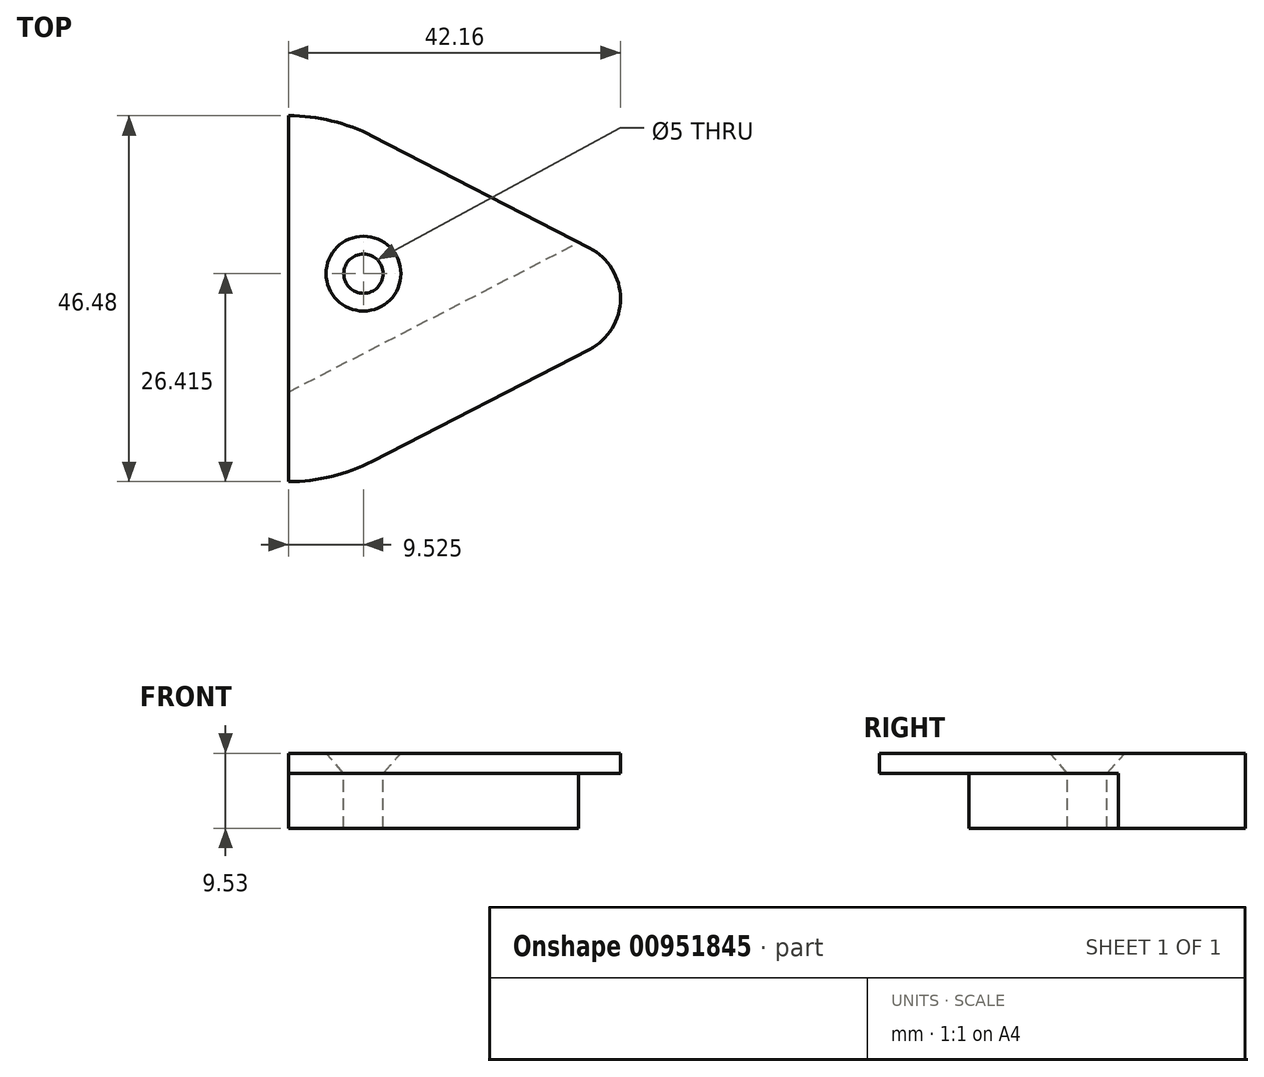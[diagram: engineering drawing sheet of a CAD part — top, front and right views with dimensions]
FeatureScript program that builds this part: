
annotation { "Feature Type Name" : "Feature", "Feature Type Description" : "" }
export const myFeature = defineFeature(function(context is Context, id is Id, definition is map)
    precondition{}
    {
        {
            var Q0;
            Q0=qCreatedBy(makeId("Top.planeOp"),FACE);
            var sketch = newSketch(context, id + "F0", { "sketchPlane" : qUnion([Q0])});
            skArc(sketch, "E0", {"start": v(0, -23.62) * mm, "mid": v(5.57, -22.96) * mm, "end": v(10.82, -21) * mm, "construction": true});
            skArc(sketch, "E1", {"start": v(38.42, -6.77) * mm, "mid": v(42.55, 0) * mm, "end": v(38.42, 6.77) * mm, "construction": true});
            skLineSegment(sketch, "E2", {"start": v(10.82, 21) * mm, "end": v(38.42, 6.77) * mm, "construction": true});
            skLineSegment(sketch, "E3", {"start": v(10.82, -21) * mm, "end": v(38.42, -6.77) * mm, "construction": true});
            skLineSegment(sketch, "E4", {"start": v(0, 23.24) * mm, "end": v(0, -23.24) * mm});
            skArc(sketch, "E5.trimOffspring", {"start": v(10.82, 21) * mm, "mid": v(5.57, 22.96) * mm, "end": v(0, 23.62) * mm, "construction": true});
            skArc(sketch, "E6.0", {"start": v(10.65, 20.66) * mm, "mid": v(5.48, 22.59) * mm, "end": v(0, 23.24) * mm});
            skArc(sketch, "E6.1", {"start": v(0, -23.24) * mm, "mid": v(5.48, -22.59) * mm, "end": v(10.65, -20.66) * mm});
            skLineSegment(sketch, "E6.2", {"start": v(10.65, -20.66) * mm, "end": v(38.24, -6.43) * mm});
            skArc(sketch, "E6.3", {"start": v(38.24, -6.43) * mm, "mid": v(42.16, 0) * mm, "end": v(38.24, 6.43) * mm});
            skLineSegment(sketch, "E6.4", {"start": v(10.65, 20.66) * mm, "end": v(38.24, 6.43) * mm});
            skSolve(sketch);
        }
        {
            var Q0;
            Q0=makeQuery(id+"F0.imprint","IMPRINT",FACE,{"disambiguationData":[TD([[makeQuery(id+"F0.imprint","IMPRINT",EDGE,{"derivedFrom":sQuery(id+"F0.wireOp",EDGE,"E4")}),1.0]])]});
            extrude(context, id + "F1", {"entities" : qUnion([Q0]), "depth" : 2.54 * mm, "offsetDistance" : 25.4 * mm});
        }
        {
            var Q0;
            Q0=makeQuery(id+"F1.opExtrude","CAP_FACE",FACE,{"disambiguationData":[OSD([sQuery(id+"F0.wireOp",EDGE,"E4"),sQuery(id+"F0.wireOp",EDGE,"E6.0"),sQuery(id+"F0.wireOp",EDGE,"E6.1"),sQuery(id+"F0.wireOp",EDGE,"E6.2"),sQuery(id+"F0.wireOp",EDGE,"E6.3"),sQuery(id+"F0.wireOp",EDGE,"E6.4")])],"isStart":true});
            var sketch = newSketch(context, id + "F2", { "sketchPlane" : qUnion([Q0])});
            skLineSegment(sketch, "E7.0", {"start": v(0, 11.86) * mm, "end": v(36.87, -7.14) * mm});
            skLineSegment(sketch, "E8", {"start": v(0, 11.86) * mm, "end": v(0, -23.24) * mm});
            skLineSegment(sketch, "E9.1", {"start": v(10.65, -20.66) * mm, "end": v(36.87, -7.14) * mm});
            skSolve(sketch);
        }
        {
            var Q0;
            Q0=makeQuery(id+"F2.imprint","IMPRINT",FACE,{"disambiguationData":[TD([[makeQuery(id+"F2.imprint","IMPRINT",EDGE,{"derivedFrom":sQuery(id+"F2.wireOp",EDGE,"E7.0")}),-1.0]])]});
            extrude(context, id + "F3", {"entities" : qUnion([Q0]), "operationType" : NewBodyOperationType.ADD, "depth" : 7 * mm, "offsetDistance" : 25.4 * mm});
        }
        {
            var Q0;
            Q0=makeQuery(id+"F1.opExtrude","CAP_FACE",FACE,{"disambiguationData":[OSD([sQuery(id+"F0.wireOp",EDGE,"E4"),sQuery(id+"F0.wireOp",EDGE,"E6.0"),sQuery(id+"F0.wireOp",EDGE,"E6.1"),sQuery(id+"F0.wireOp",EDGE,"E6.2"),sQuery(id+"F0.wireOp",EDGE,"E6.3"),sQuery(id+"F0.wireOp",EDGE,"E6.4")])],"isStart":false});
            var sketch = newSketch(context, id + "F4", { "sketchPlane" : qUnion([Q0])});
            skLineSegment(sketch, "E10", {"start": v(47.01, 0) * mm, "end": v(-13.52, 0) * mm, "construction": true});
            skPoint(sketch, "E10.startSnap0", {"position": v(42.16, 0) * mm});
            skCircle(sketch, "E11", {"center": v(34.93, 0) * mm, "radius": 13.62 * mm, "construction": true});
            skLineSegment(sketch, "E12", {"start": v(34.93, 19.32) * mm, "end": v(34.93, -21.7) * mm, "construction": true});
            skPoint(sketch, "E13", {"position": v(9.53, 3.17) * mm});
            skSolve(sketch);
        }
        {
            var Q0;
            Q0=sQuery(id+"F4.wireOp",VERTEX,"E13");
            var Q1;
            Q1=makeQuery(id+"F1.opExtrude","SWEPT_BODY",BODY,{"disambiguationData":[OSD([sQuery(id+"F0.wireOp",EDGE,"E4"),sQuery(id+"F0.wireOp",EDGE,"E6.0"),sQuery(id+"F0.wireOp",EDGE,"E6.1"),sQuery(id+"F0.wireOp",EDGE,"E6.2"),sQuery(id+"F0.wireOp",EDGE,"E6.3"),sQuery(id+"F0.wireOp",EDGE,"E6.4")])]});
            hole(context, id + "F5", {"style" : HoleStyle.C_SINK, "endStyle" : HoleEndStyle.THROUGH, "holeDiameter" : 5 * mm, "cSinkDiameter" : 9.5 * mm, "cSinkAngle" : 82 * degree, "majorDiameter" : 6.35 * mm, "isTappedThrough" : true, "tappedDepth" : 12.7 * mm, "tapClearance" : 3, "locations" : qUnion([Q0]), "scope" : qUnion([Q1])});
        }
    });
